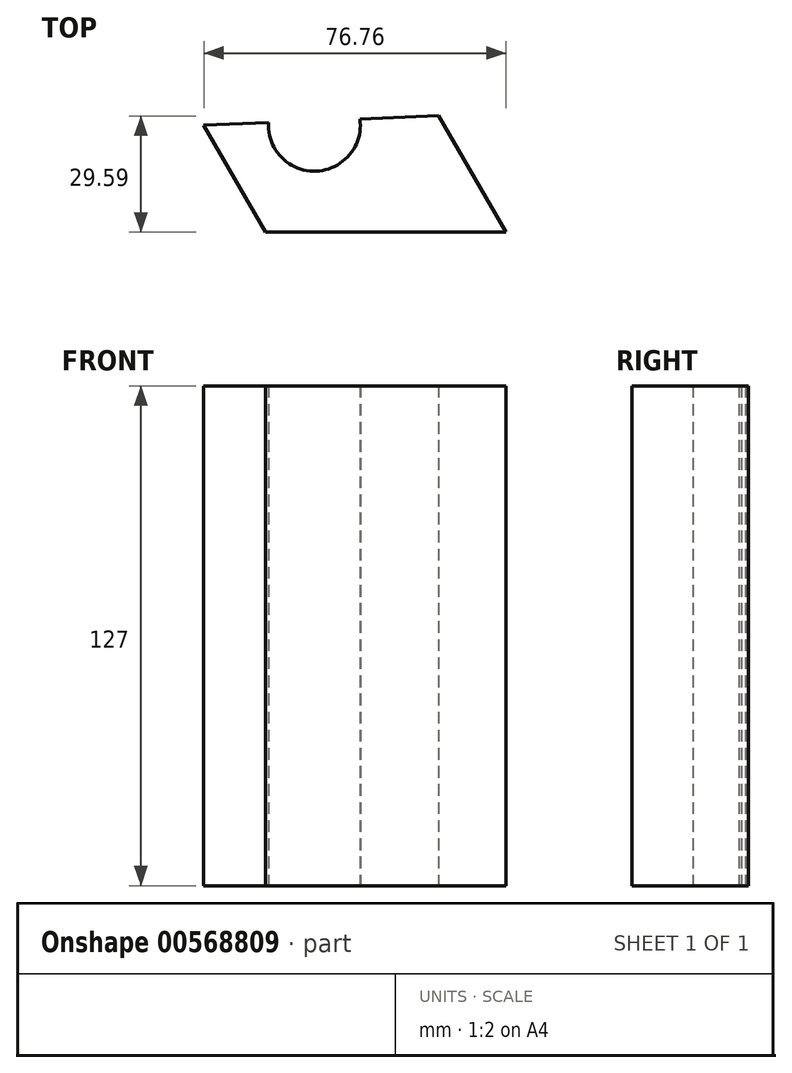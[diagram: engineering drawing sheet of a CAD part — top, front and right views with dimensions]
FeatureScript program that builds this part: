
annotation { "Feature Type Name" : "Feature", "Feature Type Description" : "" }
export const myFeature = defineFeature(function(context is Context, id is Id, definition is map)
    precondition{}
    {
        {
            var Q0;
            Q0=qCreatedBy(makeId("Top.planeOp"),FACE);
            var sketch = newSketch(context, id + "F0", { "sketchPlane" : qUnion([Q0])});
            skLineSegment(sketch, "E0", {"start": v(0, 0) * mm, "end": v(-61.08, 0) * mm});
            skLineSegment(sketch, "E1", {"start": v(-61.08, 0) * mm, "end": v(-97.44, 63.11) * mm});
            skLineSegment(sketch, "E2", {"start": v(-97.44, 63.11) * mm, "end": v(-36.44, 63.11) * mm});
            skLineSegment(sketch, "E3", {"start": v(-36.44, 63.11) * mm, "end": v(0, 0) * mm});
            skCircle(sketch, "E4", {"center": v(-48.68, 27.22) * mm, "radius": 11.69 * mm});
            skLineSegment(sketch, "E5", {"start": v(-17.09, 29.6) * mm, "end": v(-76.76, 27.22) * mm});
            skSolve(sketch);
        }
        {
            var Q0;
            Q0=makeQuery(id+"F0.imprint","IMPRINT",FACE,{"disambiguationData":[TD([[makeQuery(id+"F0.imprint","IMPRINT",EDGE,{"derivedFrom":sQuery(id+"F0.wireOp",EDGE,"E0")}),-1.0]])]});
            extrude(context, id + "F1", {"entities" : qUnion([Q0]), "depth" : 127 * mm, "offsetDistance" : 25.4 * mm});
        }
    });
